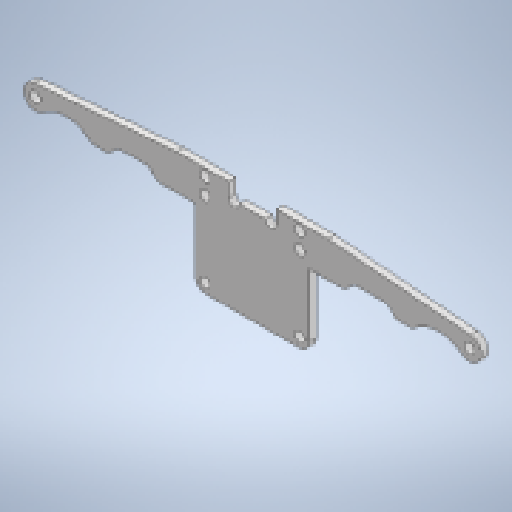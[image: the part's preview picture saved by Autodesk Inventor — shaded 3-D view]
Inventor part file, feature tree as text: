
AUTODESK INVENTOR PART (.ipt)
format: ipt  version: 2025.1 (Build 291241000, 241)  size: 344,064 bytes
history: native  units: mm
features: reference x7, other x4, extrude x3, sketch x3, fillet x2
ambient origin geometry x8: Origin, YZ Plane, XZ Plane, XY Plane, X Axis, Y Axis, Z Axis, Center Point
bodies: Body1 (feature_tree)
feature tree (19):
  other  "ソリッド1"
  extrude  "押し出し1"  Depth=2.2mm
  extrude  "押し出し4"  Depth=7.0mm
  extrude  "押し出し5"  Depth=20.0mm
  fillet  "フィレット1"  Radius=2.2mm
  fillet  "フィレット2"  Radius=16.0mm
  sketch  "スケッチ1"
  sketch  "スケッチ4"
  sketch  "スケッチ5"
  reference  "参照1"
  reference  "参照2"
  reference  "参照3"
  reference  "参照4"
  reference  "参照5"
  reference  "参照6"
  reference  "参照7"
  other  "Assembly1"
  other  "KRS2500_scale:2"
  other  "KRS2500_scale:1"
